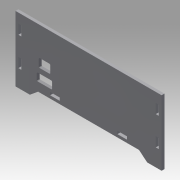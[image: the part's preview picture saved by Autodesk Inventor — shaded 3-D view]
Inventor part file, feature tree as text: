
AUTODESK INVENTOR PART (.ipt)
format: ipt  version: 2019.3 (Build 233278000, 278)  size: 171,008 bytes
history: native  units: mm
features: extrude x2, sketch x2
ambient origin geometry x8: Origin, YZ Plane, XZ Plane, XY Plane, X Axis, Y Axis, Z Axis, Center Point
bodies: Solid1 (feature_tree)
feature tree (4):
  extrude  "Extrusion1"  Depth=10.0mm
  extrude  "Extrusion2"  Depth=10.0mm
  sketch  "Sketch1"  dims[d0=3.0mm d1=10.0mm]
  sketch  "Sketch2"  dims[d2=60.0mm d3=10.0mm d4=152.0mm d5=36.0mm d6=36.0mm d7=3.1mm d8=10.0mm d9=20.0mm d10=5.0mm d11=10.0mm d12=3.0mm d13=3.0mm d14=3.0mm d15=15.0mm d16=15.0mm d17=105.0mm d18=3.0mm d19=0.0mm d20=24.09mm d21=10.0mm d22=0.0mm d23=12.0mm d24=9.0mm d28=20.6mm d29=1.0mm d30=10.75mm d31=37.25mm d32=5.0mm d33=5.0mm d34=16.0mm d35=3.0mm d36=8.0mm d37=1.0mm]
